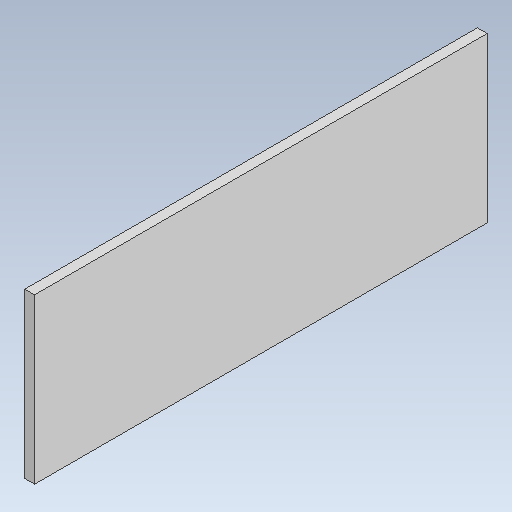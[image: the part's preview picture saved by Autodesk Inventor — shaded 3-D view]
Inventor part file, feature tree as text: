
AUTODESK INVENTOR PART (.ipt)
format: ipt  version: 2020 (Build 240168000, 168)  size: 88,576 bytes
history: native  units: mm
features: other x5, extrude x1, sketch x1
ambient origin geometry x8: Origin, YZ Plane, XZ Plane, XY Plane, X Axis, Y Axis, Z Axis, Center Point
bodies: Body1 (feature_tree)
feature tree (7):
  other  "Sólido1"
  extrude  "Extrusão1"  Depth=138.0mm TaperAngle=0.0deg
  sketch  "Esboço1"  dims[d0=50.0mm d1=138.0mm d2=0.0mm]
  other  "Referência1"
  other  "<userpath>\Desktop\rabo\3d\ela.iam"
  other  "ela.iam"
  other  "guarra_MIR_MIR:1"
